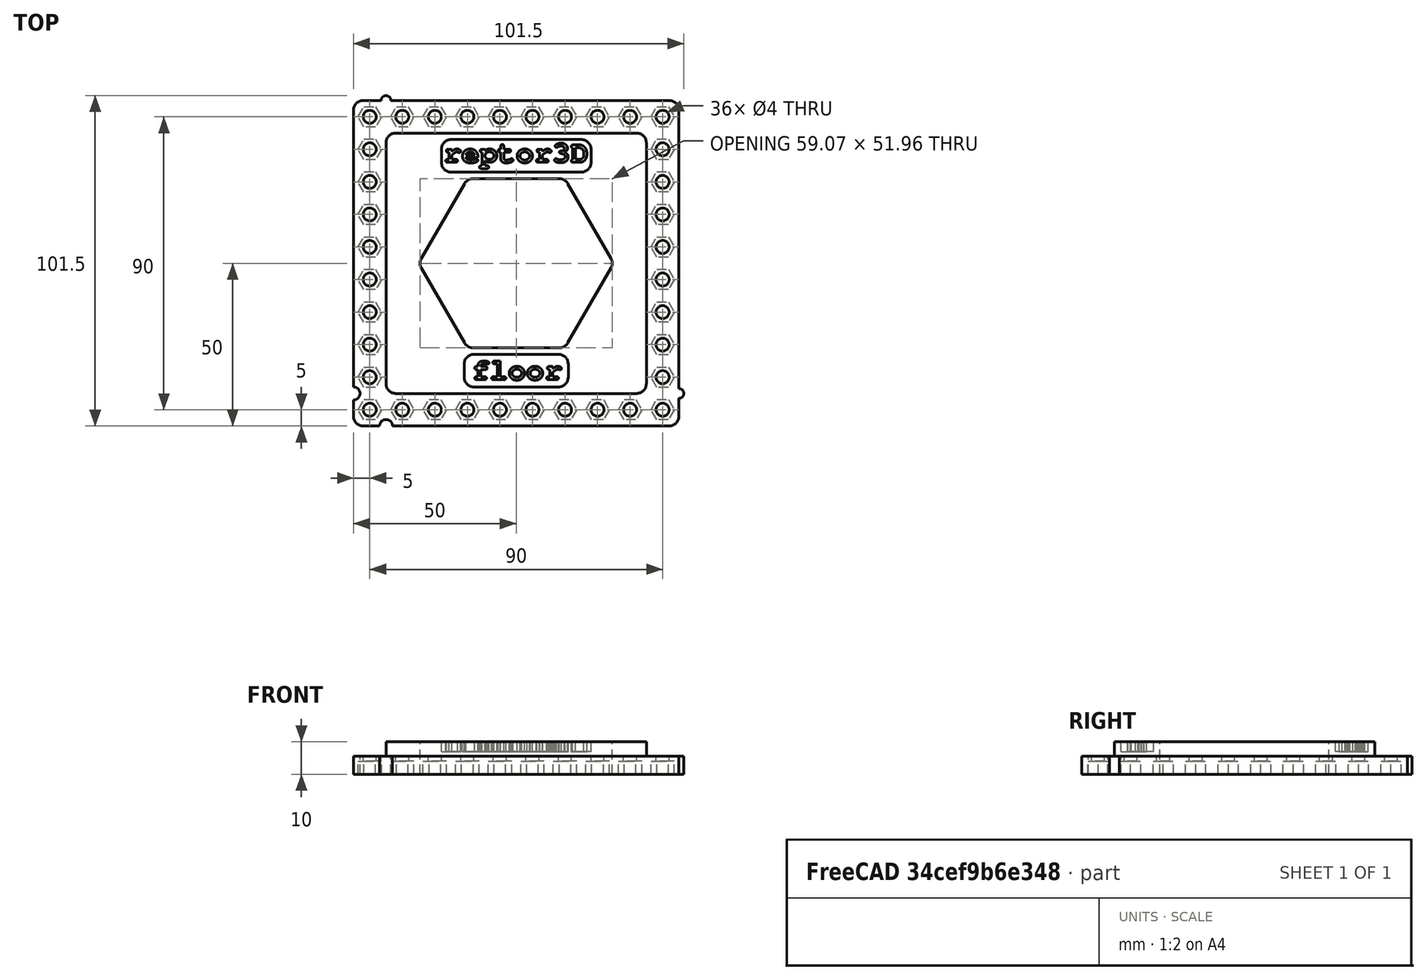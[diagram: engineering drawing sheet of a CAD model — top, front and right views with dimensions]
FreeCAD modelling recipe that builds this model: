
FCSTD DOCUMENT  (FreeCAD 0.14R3702 (Git))
Label: floor
License: CC-BY 3.0
LicenseURL: http://creativecommons.org/licenses/by/3.0/
objects: Part::Cylinder×6, Part::Box×5, Part::Extrusion×5, Part::FeaturePython×4, Part::MultiFuse×4, Part::Cut×3, Part::RegularPolygon×2, Part::Part2DObjectPython×2, Part::Fillet×2
note: 33 computed .brp shape members not serialized (recipe doc carries the construction recipe); baked Part::Feature solids carry a one-line shape summary decoded from their .brp

FEATURE [Part::Box] Box  label="s_base"
  Height = 10
  Length = 100
  Width = 100
FEATURE [Part::Box] Box001  label="h_s_groove"
  Height = 10
  Length = 120
  Placement = pos=(-10,-10,5.5) rot=(0,0,1;0rad)
  Width = 120
FEATURE [Part::Box] Box002  label="h_h_groove"
  Height = 20
  Length = 80
  Placement = pos=(10,10,0) rot=(0,0,1;0rad)
  Width = 80
FEATURE [Part::Cut] Cut  label="h_groove"
  Base = -> Box001
  Tool = -> Box002
FEATURE [Part::Cut] Cut001  label="s_base001"
  Base = -> Box
  Tool = -> Cut
FEATURE [Part::RegularPolygon] RegularPolygon  label="Regular polygon"
  Circumradius = 30
  Placement = pos=(50,50,-1) rot=(0,0,1;0rad)
  Polygon = 6
FEATURE [Part::Extrusion] Extrude  label="h_hexagon"
  Base = -> RegularPolygon
  Dir = (0,0,13)
  Placement = pos=(0,0,-1) rot=(0,0,1;0rad)
  Solid = true
FEATURE [Part::Part2DObjectPython] ShapeString  label="txt_floor"  # Draft 2D object (typed FeaturePython)
  FontFile = <path>
  Placement = pos=(36.32,14.24,6) rot=(0,0,1;0rad)
  Size = 3
  String = floor
  Tracking = 0
FEATURE [Part::Cylinder] Cylinder
  Angle = 360
  Height = 10
  Placement = pos=(5,5,-1) rot=(0,0,1;0rad)
  Radius = 2
FEATURE [Part::FeaturePython] Array  label="h_horiz_holes"  # Draft array (typed FeaturePython)
  Angle = 360
  ArrayType = 0
  Axis = (0,0,1)
  Base = -> Cylinder
  Center = (0,0,0)
  IntervalX = (10,0,0)
  IntervalY = (0,90,0)
  IntervalZ = (0,0,1)
  NumberPolar = 1
  NumberX = 10
  NumberY = 2
  NumberZ = 1
FEATURE [Part::Cylinder] Cylinder001
  Angle = 360
  Height = 10
  Placement = pos=(5,15,-1) rot=(0,0,1;0rad)
  Radius = 2
FEATURE [Part::FeaturePython] Array001  label="h_vert_holes"  # Draft array (typed FeaturePython)
  Angle = 360
  ArrayType = 0
  Axis = (0,0,1)
  Base = -> Cylinder001
  Center = (0,0,0)
  IntervalX = (90,0,0)
  IntervalY = (0,10,0)
  IntervalZ = (0,0,1)
  NumberPolar = 1
  NumberX = 2
  NumberY = 8
  NumberZ = 1
FEATURE [Part::Cylinder] Cylinder002  label="h_horiz_position"
  Angle = 360
  Height = 10
  Placement = pos=(10,0,-1) rot=(0,0,1;0rad)
  Radius = 2
FEATURE [Part::Cylinder] Cylinder003  label="s_horiz_position"
  Angle = 360
  Height = 5.5
  Placement = pos=(10,100,0) rot=(0,0,1;0rad)
  Radius = 1.5
FEATURE [Part::Cylinder] Cylinder004  label="h_vert_position"
  Angle = 360
  Height = 10
  Placement = pos=(0,10,-1) rot=(0,0,1;0rad)
  Radius = 2
FEATURE [Part::Cylinder] Cylinder005  label="s_vert_position"
  Angle = 360
  Height = 5.5
  Placement = pos=(100,10,0) rot=(0,0,1;0rad)
  Radius = 1.5
FEATURE [Part::RegularPolygon] RegularPolygon001  label="h_nut"
  Circumradius = 3.6
  Placement = pos=(5,15,-1) rot=(0,0,1;0rad)
  Polygon = 6
FEATURE [Part::Extrusion] Extrude003  label="h_nut001"
  Base = -> RegularPolygon001
  Dir = (0,0,5)
  Placement = pos=(0,-10,0) rot=(0,0,1;0rad)
  Solid = true
FEATURE [Part::FeaturePython] Array002  label="h_nut_horiz"  # Draft array (typed FeaturePython)
  Angle = 360
  ArrayType = 0
  Axis = (0,0,1)
  Base = -> Extrude003
  Center = (0,0,0)
  IntervalX = (10,0,0)
  IntervalY = (0,90,0)
  IntervalZ = (0,0,1)
  NumberPolar = 1
  NumberX = 10
  NumberY = 2
  NumberZ = 1
FEATURE [Part::Extrusion] Extrude004  label="h_bolt002"
  Base = -> RegularPolygon001
  Dir = (0,0,5)
  Solid = true
FEATURE [Part::FeaturePython] Array003  label="h_nut_vert"  # Draft array (typed FeaturePython)
  Angle = 360
  ArrayType = 0
  Axis = (0,0,1)
  Base = -> Extrude004
  Center = (0,0,0)
  IntervalX = (90,0,0)
  IntervalY = (0,10,0)
  IntervalZ = (0,0,1)
  NumberPolar = 1
  NumberX = 2
  NumberY = 8
  NumberZ = 1
FEATURE [Part::Box] Box004  label="h_groove_txt_reptor3D"
  Height = 4
  Length = 46
  Placement = pos=(27,78,7) rot=(0,0,1;0rad)
  Width = 10
FEATURE [Part::Extrusion] Extrude001  label="s_txt_floor"
  Base = -> ShapeString
  Dir = (0,0,4)
  Solid = true
FEATURE [Part::Part2DObjectPython] ShapeString001  label="txt_reptor3D"  # Draft 2D object (typed FeaturePython)
  FontFile = <path>
  Placement = pos=(27.6,81,6) rot=(0,0,1;0rad)
  Size = 4
  String = reptor3D
  Tracking = 0
FEATURE [Part::Box] Box005  label="h_groove_txt_floor"
  Height = 4
  Length = 32
  Placement = pos=(34,12,7) rot=(0,0,1;0rad)
  Width = 10
FEATURE [Part::Extrusion] Extrude005  label="s_txt_reptor3D"
  Base = -> ShapeString001
  Dir = (0,0,4)
  Solid = true
FEATURE [Part::MultiFuse] Fusion001  label="holes"
  Shapes = -> [Box005,Array003,Array,Array001,Extrude,Array002,Cylinder004,Cylinder002,Box004]
FEATURE [Part::MultiFuse] Fusion  label="s_base002"
  Shapes = -> [Cut001,Cylinder003,Cylinder005]
FEATURE [Part::Cut] Cut002  label="s_base003"
  Base = -> Fusion
  Tool = -> Fusion001
FEATURE [Part::MultiFuse] Fusion002  label="s_txt"
  Shapes = -> [Extrude005,Extrude001]
FEATURE [Part::MultiFuse] Fusion003  label="floor"
  Shapes = -> [Cut002,Fusion002]
FEATURE [Part::Fillet] Fillet
  Base = -> Fusion003
  Edges = 21 edges r=3: [Edge294,Edge298,Edge301,Edge304,Edge306,Edge308,Edge310,Edge818,Edge820,Edge821,Edge823,Edge825,Edge827,Edge845,Edge846,Edge848,Edge850,Edge853,Edge854,Edge856,Edge858]
FEATURE [Part::Fillet] Fillet001
  Base = -> Fillet
  Edges = 1 edges r=3: [Edge90]
note: 2 file-system paths scrubbed to <path> (originals preserved in the JSON sidecar)
